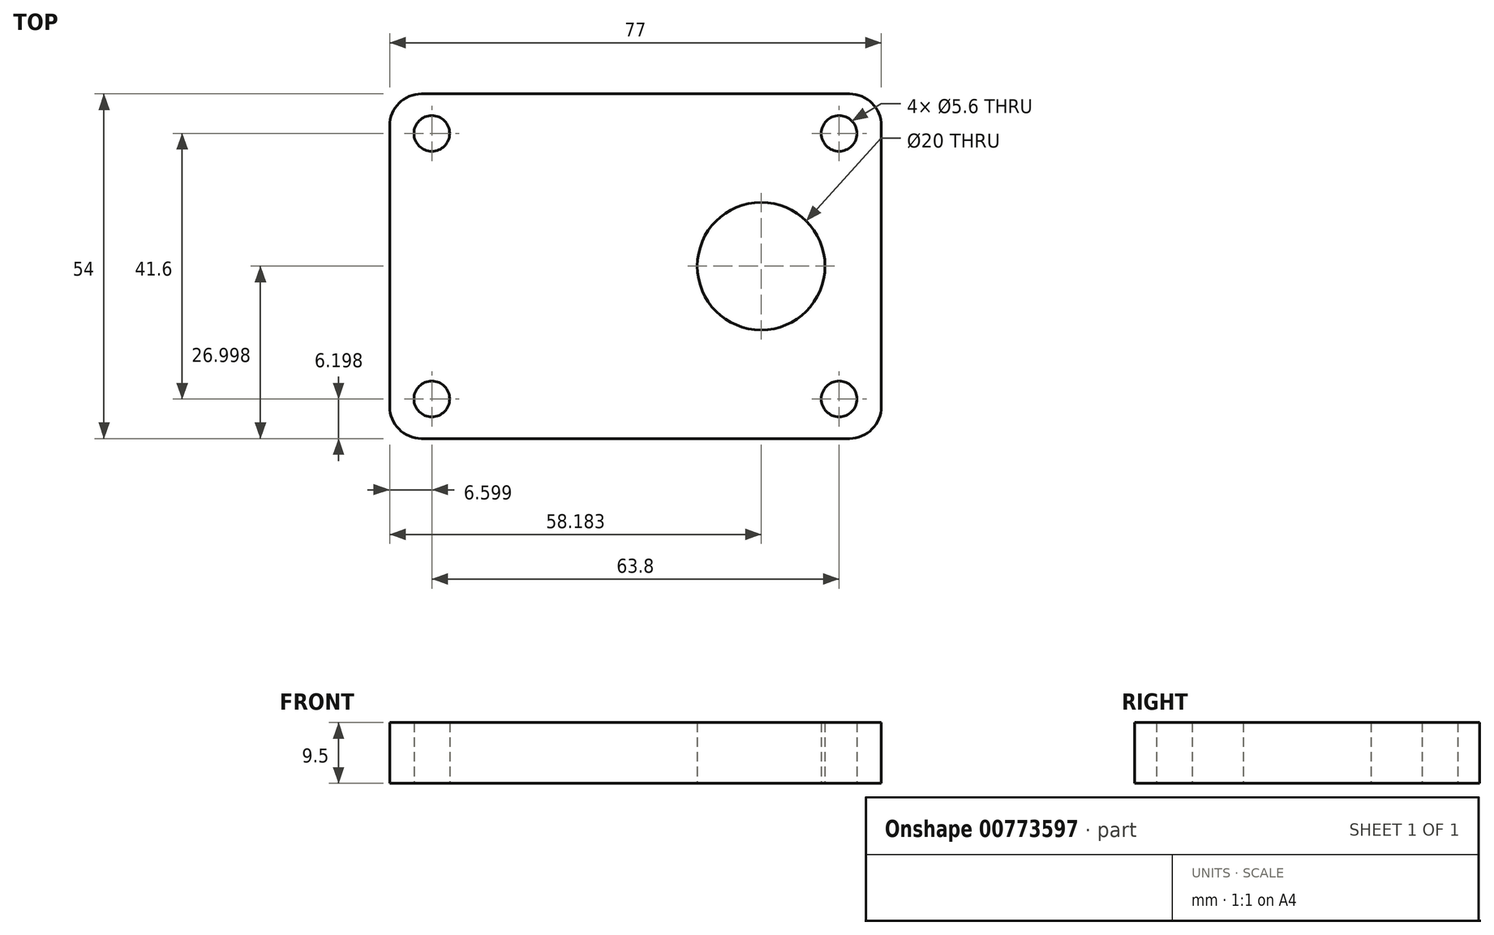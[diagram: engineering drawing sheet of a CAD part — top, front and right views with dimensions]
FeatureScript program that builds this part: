
annotation { "Feature Type Name" : "Feature", "Feature Type Description" : "" }
export const myFeature = defineFeature(function(context is Context, id is Id, definition is map)
    precondition{}
    {
        {
            var Q0;
            Q0=qCreatedBy(makeId("Top.planeOp"),FACE);
            var sketch = newSketch(context, id + "F0", { "sketchPlane" : qUnion([Q0])});
            skLineSegment(sketch, "E0.bottom", {"start": v(-36.53, 40.77) * mm, "end": v(30.47, 40.77) * mm});
            skLineSegment(sketch, "E0.top", {"start": v(-36.53, -13.23) * mm, "end": v(30.47, -13.23) * mm});
            skLineSegment(sketch, "E0.left", {"start": v(-41.53, 35.77) * mm, "end": v(-41.53, -8.23) * mm});
            skLineSegment(sketch, "E0.right", {"start": v(35.47, 35.77) * mm, "end": v(35.47, -8.23) * mm});
            skCircle(sketch, "E1", {"center": v(-34.93, 34.57) * mm, "radius": 2.8 * mm});
            skCircle(sketch, "E2", {"center": v(28.87, 34.57) * mm, "radius": 2.8 * mm});
            skCircle(sketch, "E3", {"center": v(-34.93, -7.03) * mm, "radius": 2.8 * mm});
            skCircle(sketch, "E4", {"center": v(28.87, -7.03) * mm, "radius": 2.8 * mm});
            skPoint(sketch, "E5.visualSharp", {"position": v(-41.53, 40.77) * mm});
            skArc(sketch, "E5.filletArc", {"start": v(-36.53, 40.77) * mm, "mid": v(-40.07, 39.3) * mm, "end": v(-41.53, 35.77) * mm});
            skPoint(sketch, "E6.visualSharp", {"position": v(35.47, 40.77) * mm});
            skArc(sketch, "E6.filletArc", {"start": v(35.47, 35.77) * mm, "mid": v(34, 39.3) * mm, "end": v(30.47, 40.77) * mm});
            skPoint(sketch, "E7.visualSharp", {"position": v(35.47, -13.23) * mm});
            skArc(sketch, "E7.filletArc", {"start": v(30.47, -13.23) * mm, "mid": v(34, -11.77) * mm, "end": v(35.47, -8.23) * mm});
            skPoint(sketch, "E8.visualSharp", {"position": v(-41.53, -13.23) * mm});
            skArc(sketch, "E8.filletArc", {"start": v(-41.53, -8.23) * mm, "mid": v(-40.07, -11.77) * mm, "end": v(-36.53, -13.23) * mm});
            skCircle(sketch, "E9", {"center": v(16.65, 13.77) * mm, "radius": 10 * mm});
            skPoint(sketch, "E9.centerSnap0", {"position": v(35.47, 13.77) * mm});
            skSolve(sketch);
        }
        {
            var Q0;
            Q0=qSketchRegion(id+"F0",true);
            extrude(context, id + "F1", {"entities" : qUnion([Q0]), "depth" : 9.5 * mm, "offsetDistance" : 25 * mm});
        }
    });
